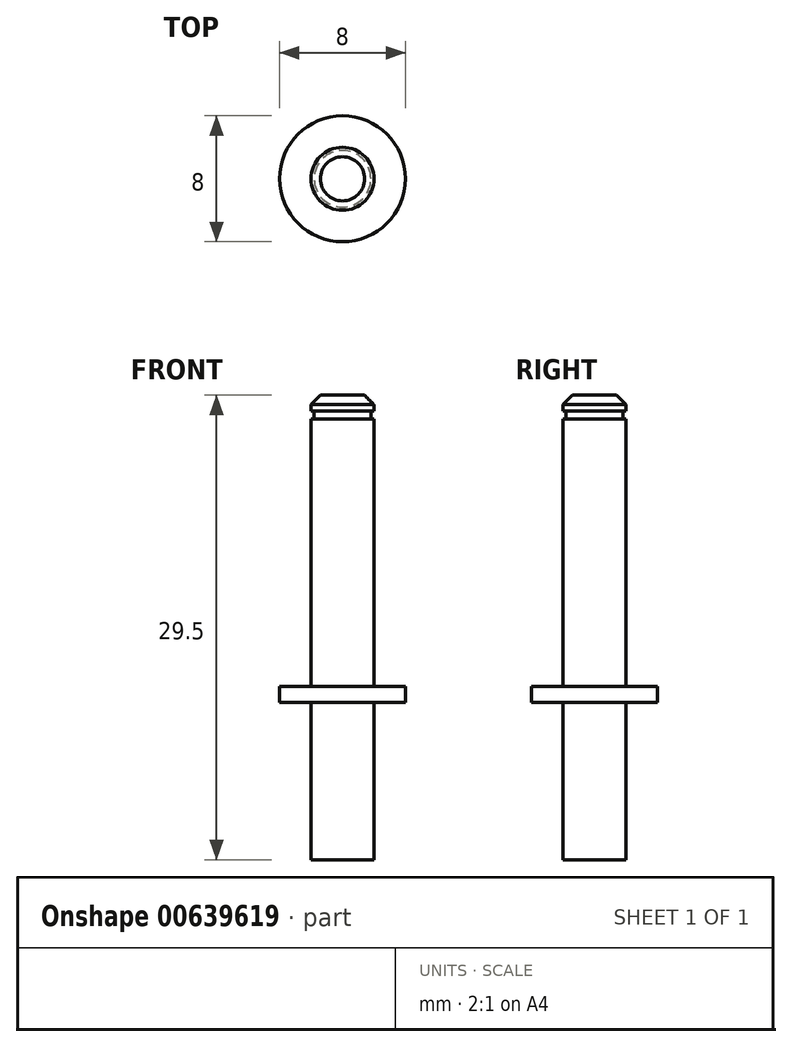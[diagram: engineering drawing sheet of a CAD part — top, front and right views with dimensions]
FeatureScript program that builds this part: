
annotation { "Feature Type Name" : "Feature", "Feature Type Description" : "" }
export const myFeature = defineFeature(function(context is Context, id is Id, definition is map)
    precondition{}
    {
        {
            var Q0;
            Q0=qCreatedBy(makeId("Top.planeOp"),FACE);
            var sketch = newSketch(context, id + "F0", { "sketchPlane" : qUnion([Q0])});
            skCircle(sketch, "E0", {"center": v(0, 0) * mm, "radius": 2 * mm});
            skSolve(sketch);
        }
        {
            var Q0;
            Q0=makeQuery(id+"F0.imprint","IMPRINT",FACE,{"disambiguationData":[TD([[makeQuery(id+"F0.imprint","IMPRINT",EDGE,{"derivedFrom":sQuery(id+"F0.wireOp",EDGE,"E0")}),1.0]])]});
            extrude(context, id + "F1", {"entities" : qUnion([Q0]), "oppositeDirection" : true, "depth" : 10 * mm, "offsetDistance" : 25 * mm});
        }
        {
            var Q0;
            Q0=qCreatedBy(makeId("Top.planeOp"),FACE);
            var sketch = newSketch(context, id + "F2", { "sketchPlane" : qUnion([Q0])});
            skCircle(sketch, "E1", {"center": v(0, 0) * mm, "radius": 4 * mm});
            skSolve(sketch);
        }
        {
            var Q0;
            Q0=makeQuery(id+"F2.imprint","IMPRINT",FACE,{"disambiguationData":[TD([[makeQuery(id+"F2.imprint","IMPRINT",EDGE,{"derivedFrom":sQuery(id+"F2.wireOp",EDGE,"E1")}),1.0]])]});
            extrude(context, id + "F3", {"entities" : qUnion([Q0]), "operationType" : NewBodyOperationType.ADD, "depth" : 1 * mm, "offsetDistance" : 25 * mm});
        }
        {
            var Q0;
            Q0=makeQuery(id+"F3.opExtrude","CAP_FACE",FACE,{"disambiguationData":[OSD([sQuery(id+"F2.wireOp",EDGE,"E1")])],"isStart":false});
            var sketch = newSketch(context, id + "F4", { "sketchPlane" : qUnion([Q0])});
            skCircle(sketch, "E2", {"center": v(0, 0) * mm, "radius": 2 * mm});
            skSolve(sketch);
        }
        {
            var Q0;
            Q0=makeQuery(id+"F4.imprint","IMPRINT",FACE,{"disambiguationData":[TD([[makeQuery(id+"F4.imprint","IMPRINT",EDGE,{"derivedFrom":sQuery(id+"F4.wireOp",EDGE,"E2")}),1.0]])]});
            extrude(context, id + "F5", {"entities" : qUnion([Q0]), "operationType" : NewBodyOperationType.ADD, "depth" : 17 * mm, "offsetDistance" : 25 * mm});
        }
        {
            var Q0;
            Q0=makeQuery(id+"F5.opExtrude","CAP_FACE",FACE,{"disambiguationData":[OSD([sQuery(id+"F4.wireOp",EDGE,"E2")])],"isStart":false});
            var sketch = newSketch(context, id + "F6", { "sketchPlane" : qUnion([Q0])});
            skCircle(sketch, "E3", {"center": v(0, 0) * mm, "radius": 1.8 * mm});
            skSolve(sketch);
        }
        {
            var Q0;
            Q0=makeQuery(id+"F6.imprint","IMPRINT",FACE,{"disambiguationData":[TD([[makeQuery(id+"F6.imprint","IMPRINT",EDGE,{"derivedFrom":sQuery(id+"F6.wireOp",EDGE,"E3")}),1.0]])]});
            extrude(context, id + "F7", {"entities" : qUnion([Q0]), "operationType" : NewBodyOperationType.ADD, "depth" : 0.5 * mm, "offsetDistance" : 25 * mm});
        }
        {
            var Q0;
            Q0=makeQuery(id+"F7.opExtrude","CAP_FACE",FACE,{"disambiguationData":[OSD([sQuery(id+"F6.wireOp",EDGE,"E3")])],"isStart":false});
            var sketch = newSketch(context, id + "F8", { "sketchPlane" : qUnion([Q0])});
            skCircle(sketch, "E4", {"center": v(0, 0) * mm, "radius": 2 * mm});
            skSolve(sketch);
        }
        {
            var Q0;
            Q0=makeQuery(id+"F8.imprint","IMPRINT",FACE,{"disambiguationData":[TD([[makeQuery(id+"F8.imprint","IMPRINT",EDGE,{"derivedFrom":sQuery(id+"F8.wireOp",EDGE,"E4")}),1.0]])]});
            var Q1;
            Q1=makeQuery(id+"F8.imprint","IMPRINT",FACE,{"disambiguationData":[TD([[makeQuery(id+"F8.imprint","IMPRINT",EDGE,{"derivedFrom":makeQuery(id+"F7.opExtrude","CAP_EDGE",EDGE,{"disambiguationData":[OSD([sQuery(id+"F6.wireOp",EDGE,"E3")])],"isStart":false})}),1.0]])]});
            extrude(context, id + "F9", {"entities" : qUnion([Q0, Q1]), "operationType" : NewBodyOperationType.ADD, "depth" : 1 * mm, "offsetDistance" : 25 * mm});
        }
        {
            var Q0;
            Q0=makeQuery(id+"F9.opExtrude","CAP_EDGE",EDGE,{"disambiguationData":[OSD([sQuery(id+"F8.wireOp",EDGE,"E4")])],"isStart":false});
            chamfer(context, id + "F10", {"entities" : qUnion([Q0]), "width" : 0.6 * mm, "tangentPropagation" : true});
        }
    });
